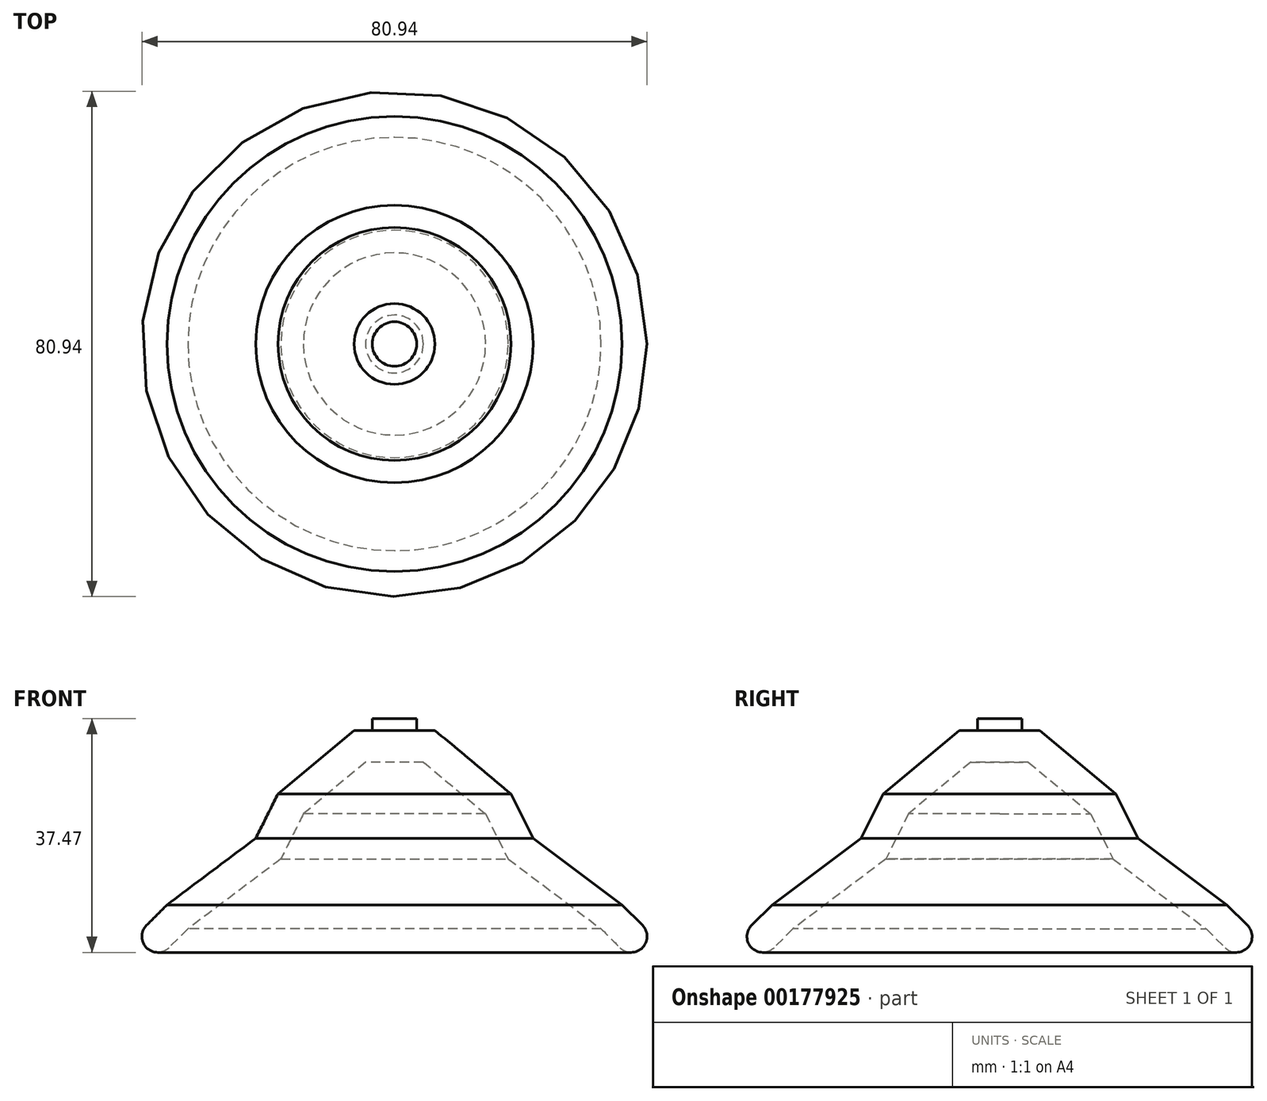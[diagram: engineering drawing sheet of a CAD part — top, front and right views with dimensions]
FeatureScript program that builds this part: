
annotation { "Feature Type Name" : "Feature", "Feature Type Description" : "" }
export const myFeature = defineFeature(function(context is Context, id is Id, definition is map)
    precondition{}
    {
        {
            var Q0;
            Q0=qCreatedBy(makeId("Top.planeOp"),FACE);
            var sketch = newSketch(context, id + "F0", { "sketchPlane" : qUnion([Q0])});
            skCircle(sketch, "E0", {"center": v(0, 0) * mm, "radius": 44.06 * mm});
            skSolve(sketch);
        }
        {
            var Q0;
            Q0=makeQuery(id+"F0.imprint","IMPRINT",FACE,{"disambiguationData":[TD([[makeQuery(id+"F0.imprint","IMPRINT",EDGE,{"derivedFrom":sQuery(id+"F0.wireOp",EDGE,"E0")}),1.0]])]});
            extrude(context, id + "F1", {"entities" : qUnion([Q0]), "depth" : 7.62 * mm});
        }
        {
            var Q0;
            Q0=makeQuery(id+"F1.opExtrude","CAP_FACE",FACE,{"disambiguationData":[OSD([sQuery(id+"F0.wireOp",EDGE,"E0")])],"isStart":false});
            chamfer(context, id + "F2", {"entities" : qUnion([Q0]), "width" : 7.62 * mm, "tangentPropagation" : true});
        }
        {
            var Q0;
            Q0=makeQuery(id+"F1.opExtrude","CAP_FACE",FACE,{"disambiguationData":[OSD([sQuery(id+"F0.wireOp",EDGE,"E0")])],"isStart":false});
            extrude(context, id + "F3", {"entities" : qUnion([Q0]), "operationType" : NewBodyOperationType.ADD, "depth" : 7.62 * mm});
        }
        {
            var Q0;
            Q0=makeQuery(id+"F3.opExtrude","CAP_FACE",FACE,{"disambiguationData":[OSD([sQuery(id+"F0.wireOp",EDGE,"E0")])],"isStart":false});
            chamfer(context, id + "F4", {"entities" : qUnion([Q0]), "chamferType" : ChamferType.TWO_OFFSETS, "width1" : 10.16 * mm, "oppositeDirection" : false, "width2" : 7.62 * mm, "tangentPropagation" : true});
        }
        {
            var Q0;
            Q0=makeQuery(id+"F3.opExtrude","CAP_FACE",FACE,{"disambiguationData":[OSD([sQuery(id+"F0.wireOp",EDGE,"E0")])],"isStart":false});
            extrude(context, id + "F5", {"entities" : qUnion([Q0]), "operationType" : NewBodyOperationType.ADD, "depth" : 10.16 * mm});
        }
        {
            var Q0;
            Q0=makeQuery(id+"F5.opExtrude","CAP_FACE",FACE,{"disambiguationData":[OSD([sQuery(id+"F0.wireOp",EDGE,"E0")])],"isStart":false});
            chamfer(context, id + "F6", {"entities" : qUnion([Q0]), "chamferType" : ChamferType.TWO_OFFSETS, "width1" : 7.62 * mm, "oppositeDirection" : false, "width2" : 15.24 * mm, "tangentPropagation" : true});
        }
        {
            var Q0;
            Q0=makeQuery(id+"F5.opExtrude","CAP_FACE",FACE,{"disambiguationData":[OSD([sQuery(id+"F0.wireOp",EDGE,"E0")])],"isStart":false});
            extrude(context, id + "F7", {"entities" : qUnion([Q0]), "operationType" : NewBodyOperationType.ADD, "depth" : 10.16 * mm});
        }
        {
            var Q0;
            Q0=makeQuery(id+"F7.opExtrude","CAP_FACE",FACE,{"disambiguationData":[OSD([sQuery(id+"F0.wireOp",EDGE,"E0")])],"isStart":false});
            chamfer(context, id + "F8", {"entities" : qUnion([Q0]), "chamferType" : ChamferType.TWO_OFFSETS, "width1" : 12.2 * mm, "oppositeDirection" : false, "width2" : 10.16 * mm, "tangentPropagation" : true});
        }
        {
            var Q0;
            Q0=makeQuery(id+"F1.opExtrude","CAP_FACE",FACE,{"disambiguationData":[OSD([sQuery(id+"F0.wireOp",EDGE,"E0")])],"isStart":true});
            shell(context, id + "F9", {"entities" : qUnion([Q0]), "thickness" : 5.08 * mm});
        }
        {
            var Q0;
            Q0=makeQuery(id+"F7.opExtrude","CAP_FACE",FACE,{"disambiguationData":[OSD([sQuery(id+"F0.wireOp",EDGE,"E0")])],"isStart":false});
            var sketch = newSketch(context, id + "F10", { "sketchPlane" : qUnion([Q0])});
            skCircle(sketch, "E1", {"center": v(0, 0) * mm, "radius": 3.56 * mm});
            skSolve(sketch);
        }
        {
            var Q0;
            Q0=makeQuery(id+"F10.imprint","IMPRINT",FACE,{"disambiguationData":[TD([[makeQuery(id+"F10.imprint","IMPRINT",EDGE,{"derivedFrom":sQuery(id+"F10.wireOp",EDGE,"E1")}),1.0]])]});
            extrude(context, id + "F11", {"entities" : qUnion([Q0]), "operationType" : NewBodyOperationType.ADD, "depth" : 1.9 * mm});
        }
        {
            var Q0;
            Q0=makeQuery(id+"F1.opExtrude","CAP_FACE",FACE,{"disambiguationData":[OSD([sQuery(id+"F0.wireOp",EDGE,"E0")])],"isStart":true});
            fillet(context, id + "F12", {"entities" : qUnion([Q0]), "radius" : 2.54 * mm, "tangentPropagation" : true, "allowEdgeOverflow" : false});
        }
    });
